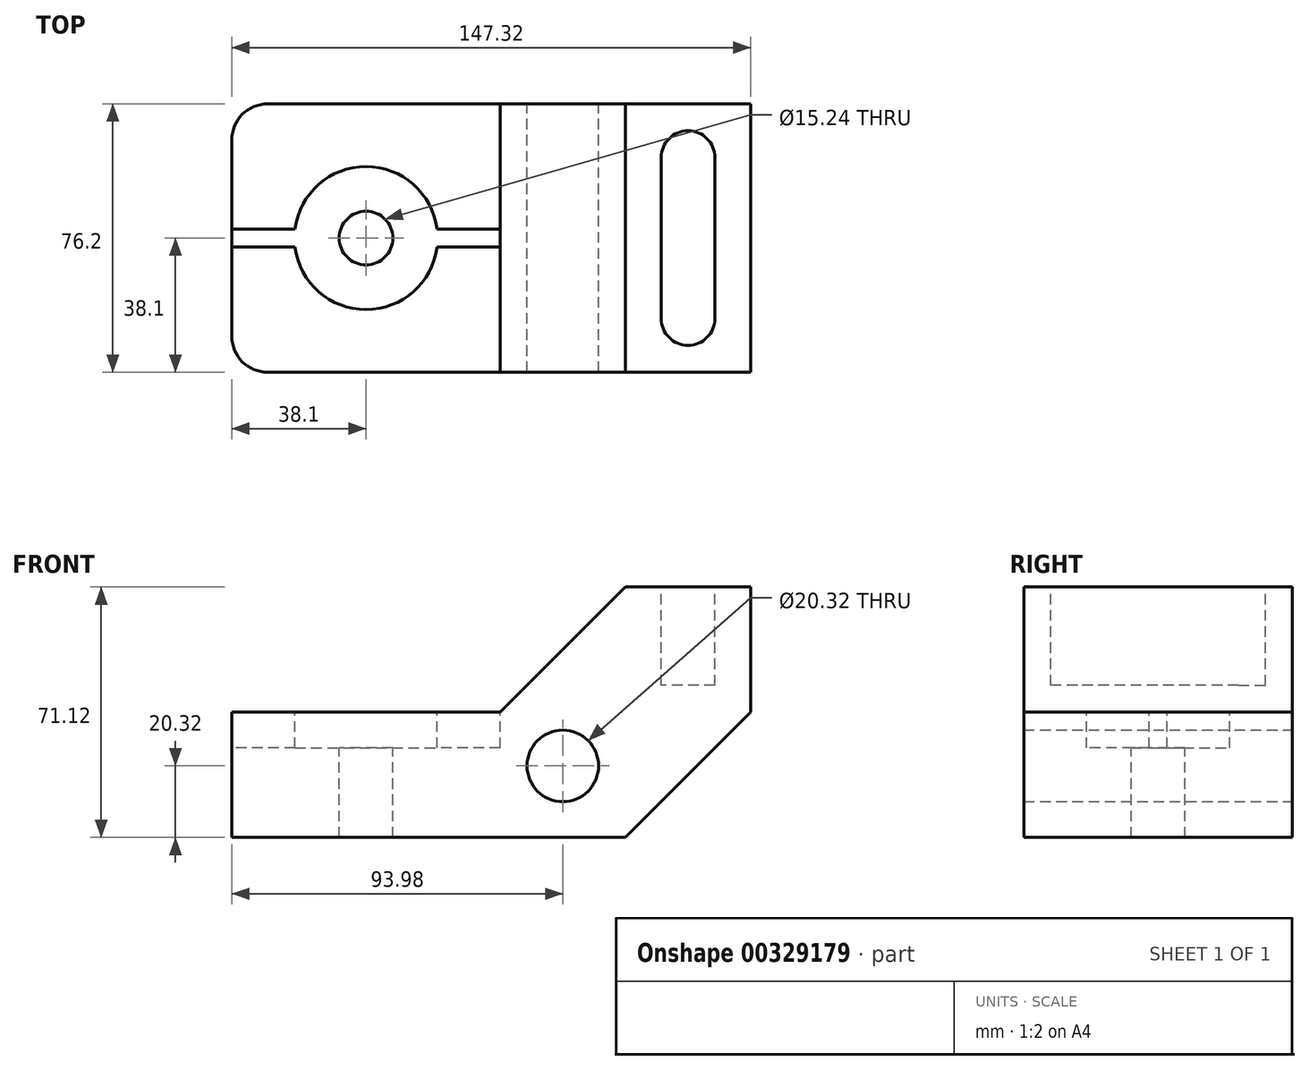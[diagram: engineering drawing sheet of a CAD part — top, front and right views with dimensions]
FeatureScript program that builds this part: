
annotation { "Feature Type Name" : "Feature", "Feature Type Description" : "" }
export const myFeature = defineFeature(function(context is Context, id is Id, definition is map)
    precondition{}
    {
        {
            var Q0;
            Q0=qCreatedBy(makeId("Front.planeOp"),FACE);
            var sketch = newSketch(context, id + "F0", { "sketchPlane" : qUnion([Q0])});
            skLineSegment(sketch, "E0", {"start": v(0, 0) * mm, "end": v(0, 35.56) * mm});
            skLineSegment(sketch, "E1", {"start": v(0, 35.56) * mm, "end": v(76.2, 35.56) * mm});
            skLineSegment(sketch, "E2", {"start": v(76.2, 35.56) * mm, "end": v(111.76, 71.12) * mm});
            skLineSegment(sketch, "E3", {"start": v(111.76, 71.12) * mm, "end": v(147.32, 71.12) * mm});
            skLineSegment(sketch, "E4", {"start": v(147.32, 71.12) * mm, "end": v(147.32, 35.56) * mm});
            skLineSegment(sketch, "E5", {"start": v(147.32, 35.56) * mm, "end": v(111.76, 0) * mm});
            skLineSegment(sketch, "E6", {"start": v(111.76, 0) * mm, "end": v(0, 0) * mm});
            skLineSegment(sketch, "E7", {"start": v(111.76, 0) * mm, "end": v(147.32, 0) * mm, "construction": true});
            skLineSegment(sketch, "E8", {"start": v(147.32, 0) * mm, "end": v(147.32, 35.56) * mm, "construction": true});
            skCircle(sketch, "E9", {"center": v(93.98, 20.32) * mm, "radius": 10.16 * mm});
            skSolve(sketch);
        }
        {
            var Q0;
            Q0 = qSketchRegion(id + "F0", true);
            extrude(context, id + "F1", {"entities" : qUnion([Q0]), "depth" : 76.2 * mm});
        }
        {
            var Q0;
            Q0=makeQuery(id+"F1.opExtrude","SWEPT_FACE",FACE,{"disambiguationData":[OSD([sQuery(id+"F0.wireOp",EDGE,"E1")])]});
            var sketch = newSketch(context, id + "F2", { "sketchPlane" : qUnion([Q0])});
            skPoint(sketch, "E10", {"position": v(38.1, -38.1) * mm});
            skLineSegment(sketch, "E11.bottom", {"start": v(76.2, -35.56) * mm, "end": v(0, -35.56) * mm});
            skLineSegment(sketch, "E11.top", {"start": v(76.2, -40.64) * mm, "end": v(0, -40.64) * mm});
            skLineSegment(sketch, "E11.left", {"start": v(76.2, -35.56) * mm, "end": v(76.2, -40.64) * mm});
            skLineSegment(sketch, "E11.right", {"start": v(0, -35.56) * mm, "end": v(0, -40.64) * mm});
            skPoint(sketch, "E12", {"position": v(0, -38.1) * mm});
            skSolve(sketch);
        }
        {
            var Q0;
            Q0=sQuery(id+"F2.wireOp",VERTEX,"E10");
            var Q1;
            Q1=makeQuery(id+"F1.opExtrude","SWEPT_BODY",BODY,{"disambiguationData":[OSD([sQuery(id+"F0.wireOp",EDGE,"E0"),sQuery(id+"F0.wireOp",EDGE,"E1"),sQuery(id+"F0.wireOp",EDGE,"E2"),sQuery(id+"F0.wireOp",EDGE,"E3"),sQuery(id+"F0.wireOp",EDGE,"E4"),sQuery(id+"F0.wireOp",EDGE,"E5"),sQuery(id+"F0.wireOp",EDGE,"E6"),sQuery(id+"F0.wireOp",EDGE,"E9")])]});
            hole(context, id + "F3", {"style" : HoleStyle.C_BORE, "endStyle" : HoleEndStyle.THROUGH, "holeDiameter" : 15.24 * mm, "cBoreDiameter" : 40.64 * mm, "cBoreDepth" : 10.16 * mm, "tappedDepth" : 12.7 * mm, "tapClearance" : 3, "locations" : qUnion([Q0]), "scope" : qUnion([Q1])});
        }
        {
            var Q0;
            Q0 = qSketchRegion(id + "F2", true);
            extrude(context, id + "F4", {"entities" : qUnion([Q0]), "operationType" : NewBodyOperationType.REMOVE, "oppositeDirection" : true, "depth" : 10.16 * mm});
        }
        {
            var Q0;
            Q0=makeQuery(id+"F1.opExtrude","CAP_EDGE",EDGE,{"disambiguationData":[OSD([sQuery(id+"F0.wireOp",EDGE,"E0")])],"isStart":false});
            var Q1;
            Q1=makeQuery(id+"F1.opExtrude","CAP_EDGE",EDGE,{"disambiguationData":[OSD([sQuery(id+"F0.wireOp",EDGE,"E0")])],"isStart":true});
            fillet(context, id + "F5", {"entities" : qUnion([Q0, Q1]), "radius" : 10.16 * mm, "tangentPropagation" : true, "allowEdgeOverflow" : false});
        }
        {
            var Q0;
            Q0=makeQuery(id+"F1.opExtrude","SWEPT_FACE",FACE,{"disambiguationData":[OSD([sQuery(id+"F0.wireOp",EDGE,"E3")])]});
            var sketch = newSketch(context, id + "F6", { "sketchPlane" : qUnion([Q0])});
            skLineSegment(sketch, "E13", {"start": v(129.54, -15.24) * mm, "end": v(129.54, -60.96) * mm});
            skArc(sketch, "E14.0.startCap", {"start": v(121.92, -15.24) * mm, "mid": v(129.54, -7.62) * mm, "end": v(137.16, -15.24) * mm});
            skArc(sketch, "E14.0.endCap", {"start": v(137.16, -60.96) * mm, "mid": v(129.54, -68.58) * mm, "end": v(121.92, -60.96) * mm});
            skLineSegment(sketch, "E14.0.left", {"start": v(137.16, -15.24) * mm, "end": v(137.16, -60.96) * mm});
            skLineSegment(sketch, "E14.0.right", {"start": v(121.92, -15.24) * mm, "end": v(121.92, -60.96) * mm});
            skSolve(sketch);
        }
        {
            var Q0;
            Q0 = qSketchRegion(id + "F6", true);
            extrude(context, id + "F7", {"entities" : qUnion([Q0]), "operationType" : NewBodyOperationType.REMOVE, "oppositeDirection" : true, "depth" : 27.94 * mm});
        }
    });
